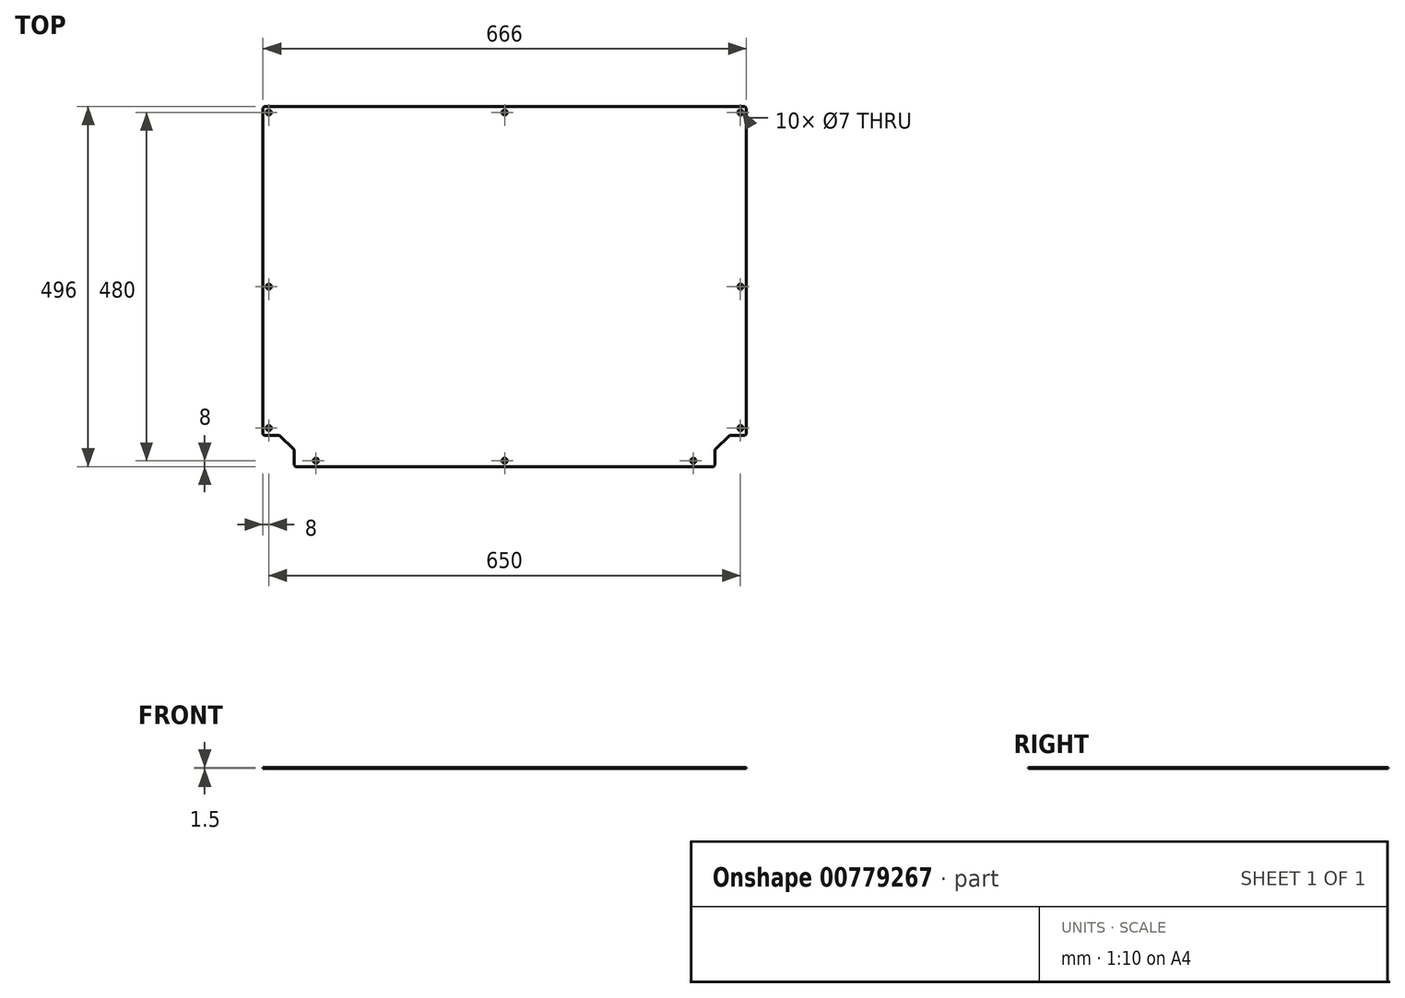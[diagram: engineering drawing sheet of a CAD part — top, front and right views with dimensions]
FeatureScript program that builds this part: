
annotation { "Feature Type Name" : "Feature", "Feature Type Description" : "" }
export const myFeature = defineFeature(function(context is Context, id is Id, definition is map)
    precondition{}
    {
        {
            var Q0;
            Q0=qCreatedBy(makeId("Top.planeOp"),FACE);
            var sketch = newSketch(context, id + "F0", { "sketchPlane" : qUnion([Q0])});
            skLineSegment(sketch, "E0.bottom", {"start": v(333, -248) * mm, "end": v(-333, -248) * mm});
            skLineSegment(sketch, "E0.top", {"start": v(333, 248) * mm, "end": v(-333, 248) * mm});
            skLineSegment(sketch, "E0.left", {"start": v(333, -248) * mm, "end": v(333, 248) * mm});
            skLineSegment(sketch, "E0.right", {"start": v(-333, -248) * mm, "end": v(-333, 248) * mm});
            skPoint(sketch, "E0.middle", {"position": v(0, 0) * mm});
            skSolve(sketch);
        }
        {
            var Q0;
            Q0=makeQuery(id+"F0.imprint","IMPRINT",FACE,{"disambiguationData":[TD([[makeQuery(id+"F0.imprint","IMPRINT",EDGE,{"derivedFrom":sQuery(id+"F0.wireOp",EDGE,"E0.bottom")}),-1.0]])]});
            extrude(context, id + "F1", {"entities" : qUnion([Q0]), "depth" : 1.5 * mm, "offsetDistance" : 25 * mm});
        }
        {
            var Q0;
            Q0=makeQuery(id+"F1.opExtrude","CAP_FACE",FACE,{"disambiguationData":[OSD([sQuery(id+"F0.wireOp",EDGE,"E0.bottom"),sQuery(id+"F0.wireOp",EDGE,"E0.top"),sQuery(id+"F0.wireOp",EDGE,"E0.left"),sQuery(id+"F0.wireOp",EDGE,"E0.right")])],"isStart":false});
            var sketch = newSketch(context, id + "F2", { "sketchPlane" : qUnion([Q0])});
            skCircle(sketch, "E1", {"center": v(-325, 240) * mm, "radius": 3.5 * mm});
            skPoint(sketch, "E2.startSnap0", {"position": v(0, 248) * mm});
            skCircle(sketch, "E3", {"center": v(0, 240) * mm, "radius": 3.5 * mm});
            skCircle(sketch, "E4", {"center": v(325, 240) * mm, "radius": 3.5 * mm});
            skCircle(sketch, "E5", {"center": v(325, 0) * mm, "radius": 3.5 * mm});
            skCircle(sketch, "E6", {"center": v(325, -195) * mm, "radius": 3.5 * mm});
            skCircle(sketch, "E7", {"center": v(260, -240) * mm, "radius": 3.5 * mm});
            skCircle(sketch, "E8", {"center": v(-260, -240) * mm, "radius": 3.5 * mm});
            skCircle(sketch, "E9", {"center": v(-325, -195) * mm, "radius": 3.5 * mm});
            skCircle(sketch, "E10", {"center": v(-325, 0) * mm, "radius": 3.5 * mm});
            skCircle(sketch, "E11", {"center": v(0, -240) * mm, "radius": 3.5 * mm});
            skSolve(sketch);
        }
        {
            var Q0;
            Q0 = qSketchRegion(id + "F2", true);
            extrude(context, id + "F3", {"entities" : qUnion([Q0]), "operationType" : NewBodyOperationType.REMOVE, "endBound" : BoundingType.UP_TO_NEXT, "oppositeDirection" : true, "depth" : 25 * mm, "offsetDistance" : 25 * mm});
        }
        {
            var Q0;
            Q0=makeQuery(id+"F1.opExtrude","CAP_FACE",FACE,{"disambiguationData":[OSD([sQuery(id+"F0.wireOp",EDGE,"E0.bottom"),sQuery(id+"F0.wireOp",EDGE,"E0.top"),sQuery(id+"F0.wireOp",EDGE,"E0.left"),sQuery(id+"F0.wireOp",EDGE,"E0.right")])],"isStart":false});
            var sketch = newSketch(context, id + "F4", { "sketchPlane" : qUnion([Q0])});
            skLineSegment(sketch, "E12", {"start": v(-333, 248) * mm, "end": v(-333, 246) * mm});
            skLineSegment(sketch, "E13", {"start": v(-333, 246) * mm, "end": v(-331, 248) * mm});
            skLineSegment(sketch, "E14", {"start": v(-331, 248) * mm, "end": v(-333, 248) * mm});
            skLineSegment(sketch, "E15", {"start": v(-333, -248) * mm, "end": v(-290, -248) * mm});
            skLineSegment(sketch, "E16", {"start": v(-290, -248) * mm, "end": v(-290, -205) * mm});
            skLineSegment(sketch, "E17", {"start": v(-290, -205) * mm, "end": v(-333, -205) * mm});
            skLineSegment(sketch, "E18", {"start": v(-333, -205) * mm, "end": v(-333, -248) * mm});
            skLineSegment(sketch, "E19", {"start": v(-310, -205) * mm, "end": v(-290, -225) * mm});
            skLineSegment(sketch, "E20", {"start": v(-290, -246) * mm, "end": v(-288, -248) * mm});
            skLineSegment(sketch, "E21", {"start": v(-333, -203) * mm, "end": v(-331, -205) * mm});
            skSolve(sketch);
        }
        {
            var Q0;
            {var subQ2=sQuery(id+"F4.wireOp",EDGE,"E13");Q0=makeQuery(id+"F4.imprint","IMPRINT",FACE,{"disambiguationData":[TD([[makeQuery(id+"F4.imprint","IMPRINT",EDGE,{"derivedFrom":subQ2}),-1.0]])]});}
            var sketch = newSketch(context, id + "F5", { "sketchPlane" : qUnion([Q0])});
            skPoint(sketch, "E22.0", {"position": v(-332, -204) * mm});
            skLineSegment(sketch, "E23.0", {"start": v(-333, 248) * mm, "end": v(-333, 246) * mm});
            skLineSegment(sketch, "E23.1", {"start": v(-333, 246) * mm, "end": v(-331, 248) * mm});
            skLineSegment(sketch, "E23.2", {"start": v(-331, 248) * mm, "end": v(-333, 248) * mm});
            skLineSegment(sketch, "E23.3", {"start": v(-333, -248) * mm, "end": v(-290, -248) * mm});
            skLineSegment(sketch, "E23.4", {"start": v(-290, -246) * mm, "end": v(-290, -225) * mm});
            skLineSegment(sketch, "E23.5", {"start": v(-310, -205) * mm, "end": v(-331, -205) * mm});
            skLineSegment(sketch, "E23.6", {"start": v(-333, -205) * mm, "end": v(-333, -248) * mm});
            skLineSegment(sketch, "E23.7", {"start": v(-310, -205) * mm, "end": v(-290, -225) * mm});
            skLineSegment(sketch, "E23.8", {"start": v(-290, -246) * mm, "end": v(-288, -248) * mm});
            skLineSegment(sketch, "E23.9", {"start": v(-333, -203) * mm, "end": v(-331, -205) * mm});
            skPoint(sketch, "E24.orphan", {"position": v(-333, -205) * mm});
            skPoint(sketch, "E25.orphan", {"position": v(-290, -248) * mm});
            skLineSegment(sketch, "E26", {"start": v(-333, -205) * mm, "end": v(-333, -203) * mm});
            skLineSegment(sketch, "E27", {"start": v(-290, -248) * mm, "end": v(-288, -248) * mm});
            skLineSegment(sketch, "E28", {"start": v(0, 294.65) * mm, "end": v(0, -314.64) * mm, "construction": true});
            skLineSegment(sketch, "E29.MirrorCS", {"start": v(331, 248) * mm, "end": v(333, 248) * mm});
            skLineSegment(sketch, "E30.MirrorCS", {"start": v(333, 248) * mm, "end": v(333, 246) * mm});
            skLineSegment(sketch, "E31.MirrorCS", {"start": v(333, 246) * mm, "end": v(331, 248) * mm});
            skLineSegment(sketch, "E32.MirrorCS", {"start": v(333, -203) * mm, "end": v(331, -205) * mm});
            skLineSegment(sketch, "E33.MirrorCS", {"start": v(333, -205) * mm, "end": v(333, -203) * mm});
            skLineSegment(sketch, "E34.MirrorCS", {"start": v(290, -246) * mm, "end": v(288, -248) * mm});
            skLineSegment(sketch, "E35.MirrorCS", {"start": v(290, -248) * mm, "end": v(288, -248) * mm});
            skLineSegment(sketch, "E36.MirrorCS", {"start": v(310, -205) * mm, "end": v(290, -225) * mm});
            skLineSegment(sketch, "E37.MirrorCS", {"start": v(333, -205) * mm, "end": v(333, -248) * mm});
            skLineSegment(sketch, "E38.MirrorCS", {"start": v(310, -205) * mm, "end": v(331, -205) * mm});
            skLineSegment(sketch, "E39.MirrorCS", {"start": v(290, -246) * mm, "end": v(290, -225) * mm});
            skLineSegment(sketch, "E40.MirrorCS", {"start": v(333, -248) * mm, "end": v(290, -248) * mm});
            skPoint(sketch, "E41.MirrorP", {"position": v(332, -204) * mm});
            skPoint(sketch, "E42.MirrorP", {"position": v(290, -248) * mm});
            skPoint(sketch, "E43.MirrorP", {"position": v(333, -205) * mm});
            skSolve(sketch);
        }
        {
            var Q0;
            Q0 = qSketchRegion(id + "F5", true);
            extrude(context, id + "F6", {"entities" : qUnion([Q0]), "operationType" : NewBodyOperationType.REMOVE, "endBound" : BoundingType.UP_TO_NEXT, "oppositeDirection" : true, "depth" : 25 * mm, "offsetDistance" : 25 * mm});
        }
    });
